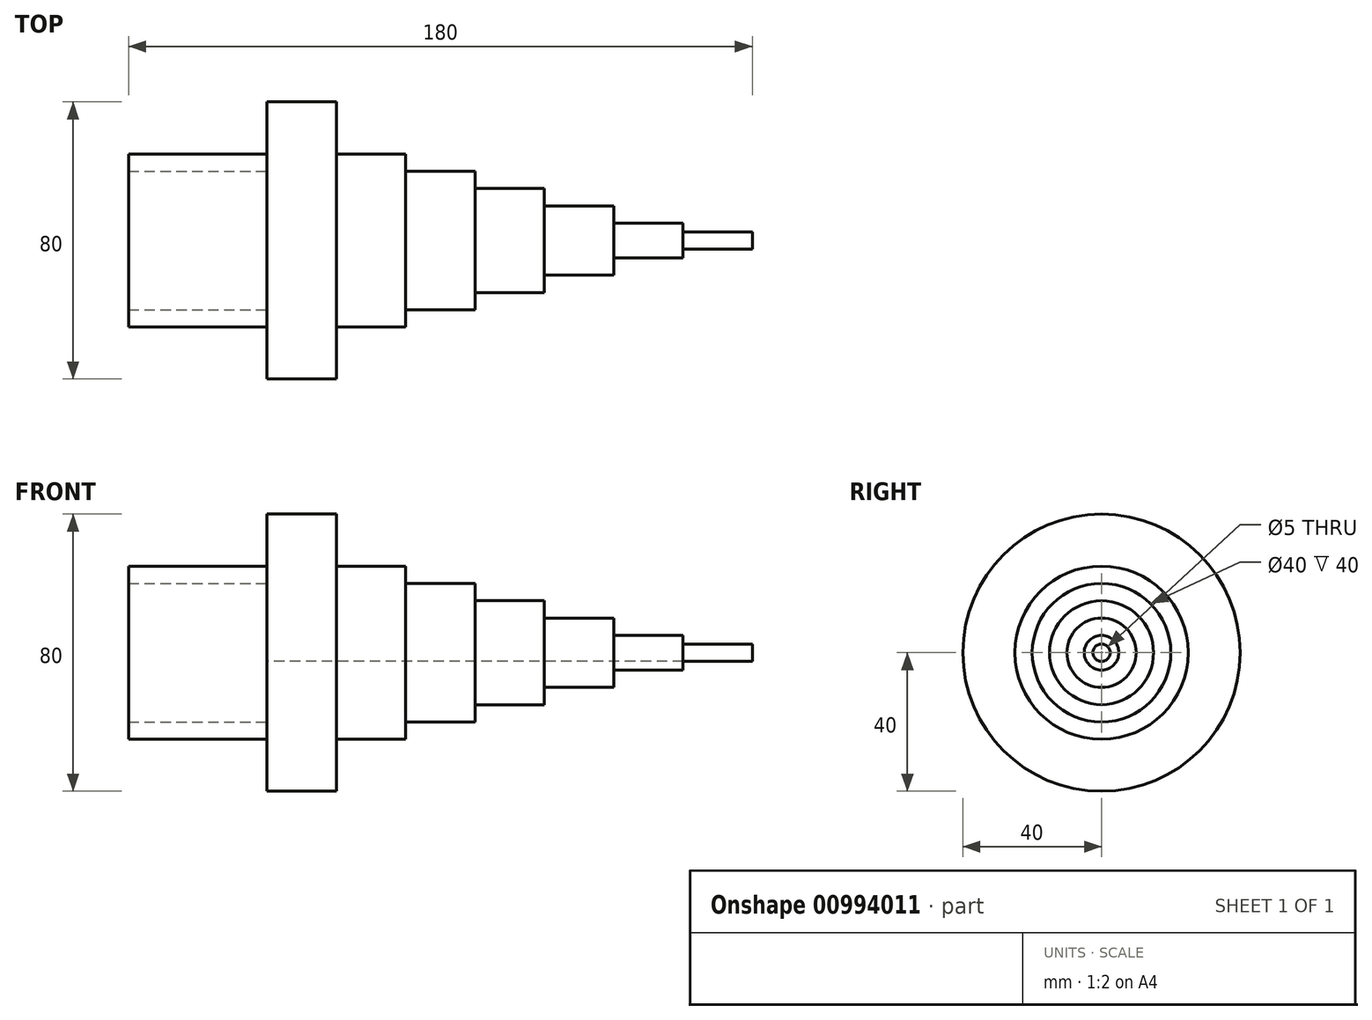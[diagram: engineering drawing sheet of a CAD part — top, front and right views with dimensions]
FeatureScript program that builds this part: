
annotation { "Feature Type Name" : "Feature", "Feature Type Description" : "" }
export const myFeature = defineFeature(function(context is Context, id is Id, definition is map)
    precondition{}
    {
        {
            var Q0;
            Q0=qCreatedBy(makeId("Right.planeOp"),FACE);
            var sketch = newSketch(context, id + "F0", { "sketchPlane" : qUnion([Q0])});
            skCircle(sketch, "E0", {"center": v(0, 0) * mm, "radius": 2.5 * mm});
            skCircle(sketch, "E1", {"center": v(0, 0) * mm, "radius": 5 * mm});
            skCircle(sketch, "E2", {"center": v(0, 0) * mm, "radius": 10 * mm});
            skCircle(sketch, "E3", {"center": v(0, 0) * mm, "radius": 15 * mm});
            skCircle(sketch, "E4", {"center": v(0, 0) * mm, "radius": 20 * mm});
            skCircle(sketch, "E5", {"center": v(0, 0) * mm, "radius": 25 * mm});
            skCircle(sketch, "E6", {"center": v(0, 0) * mm, "radius": 40 * mm});
            skSolve(sketch);
        }
        {
            var Q0;
            Q0=makeQuery(id+"F0.imprint","IMPRINT",FACE,{"disambiguationData":[TD([[makeQuery(id+"F0.imprint","IMPRINT",EDGE,{"derivedFrom":sQuery(id+"F0.wireOp",EDGE,"E0")}),1.0]])]});
            extrude(context, id + "F1", {"entities" : qUnion([Q0]), "depth" : 140 * mm, "offsetDistance" : 25 * mm});
        }
        {
            var Q0;
            Q0=makeQuery(id+"F0.imprint","IMPRINT",FACE,{"disambiguationData":[TD([[makeQuery(id+"F0.imprint","IMPRINT",EDGE,{"derivedFrom":sQuery(id+"F0.wireOp",EDGE,"E0")}),-1.0]])]});
            extrude(context, id + "F2", {"entities" : qUnion([Q0]), "depth" : 120 * mm, "offsetDistance" : 25 * mm});
        }
        {
            var Q0;
            Q0=makeQuery(id+"F0.imprint","IMPRINT",FACE,{"disambiguationData":[TD([[makeQuery(id+"F0.imprint","IMPRINT",EDGE,{"derivedFrom":sQuery(id+"F0.wireOp",EDGE,"E1")}),-1.0]])]});
            extrude(context, id + "F3", {"entities" : qUnion([Q0]), "operationType" : NewBodyOperationType.ADD, "depth" : 100 * mm, "offsetDistance" : 25 * mm});
        }
        {
            var Q0;
            Q0=makeQuery(id+"F0.imprint","IMPRINT",FACE,{"disambiguationData":[TD([[makeQuery(id+"F0.imprint","IMPRINT",EDGE,{"derivedFrom":sQuery(id+"F0.wireOp",EDGE,"E2")}),-1.0]])]});
            extrude(context, id + "F4", {"entities" : qUnion([Q0]), "operationType" : NewBodyOperationType.ADD, "depth" : 80 * mm, "offsetDistance" : 25 * mm});
        }
        {
            var Q0;
            Q0=makeQuery(id+"F0.imprint","IMPRINT",FACE,{"disambiguationData":[TD([[makeQuery(id+"F0.imprint","IMPRINT",EDGE,{"derivedFrom":sQuery(id+"F0.wireOp",EDGE,"E3")}),-1.0]])]});
            extrude(context, id + "F5", {"entities" : qUnion([Q0]), "operationType" : NewBodyOperationType.ADD, "depth" : 60 * mm, "offsetDistance" : 25 * mm});
        }
        {
            var Q0;
            Q0=makeQuery(id+"F0.imprint","IMPRINT",FACE,{"disambiguationData":[TD([[makeQuery(id+"F0.imprint","IMPRINT",EDGE,{"derivedFrom":sQuery(id+"F0.wireOp",EDGE,"E4")}),-1.0]])]});
            extrude(context, id + "F6", {"entities" : qUnion([Q0]), "operationType" : NewBodyOperationType.ADD, "depth" : 40 * mm, "offsetDistance" : 25 * mm});
        }
        {
            var Q0;
            Q0=makeQuery(id+"F0.imprint","IMPRINT",FACE,{"disambiguationData":[TD([[makeQuery(id+"F0.imprint","IMPRINT",EDGE,{"derivedFrom":sQuery(id+"F0.wireOp",EDGE,"E5")}),-1.0]])]});
            extrude(context, id + "F7", {"entities" : qUnion([Q0]), "operationType" : NewBodyOperationType.ADD, "depth" : 20 * mm, "offsetDistance" : 25 * mm});
        }
        {
            var Q0;
            Q0=makeQuery(id+"F0.imprint","IMPRINT",FACE,{"disambiguationData":[TD([[makeQuery(id+"F0.imprint","IMPRINT",EDGE,{"derivedFrom":sQuery(id+"F0.wireOp",EDGE,"E4")}),-1.0]])]});
            extrude(context, id + "F8", {"entities" : qUnion([Q0]), "oppositeDirection" : true, "depth" : 40 * mm, "offsetDistance" : 25 * mm});
        }
    });
